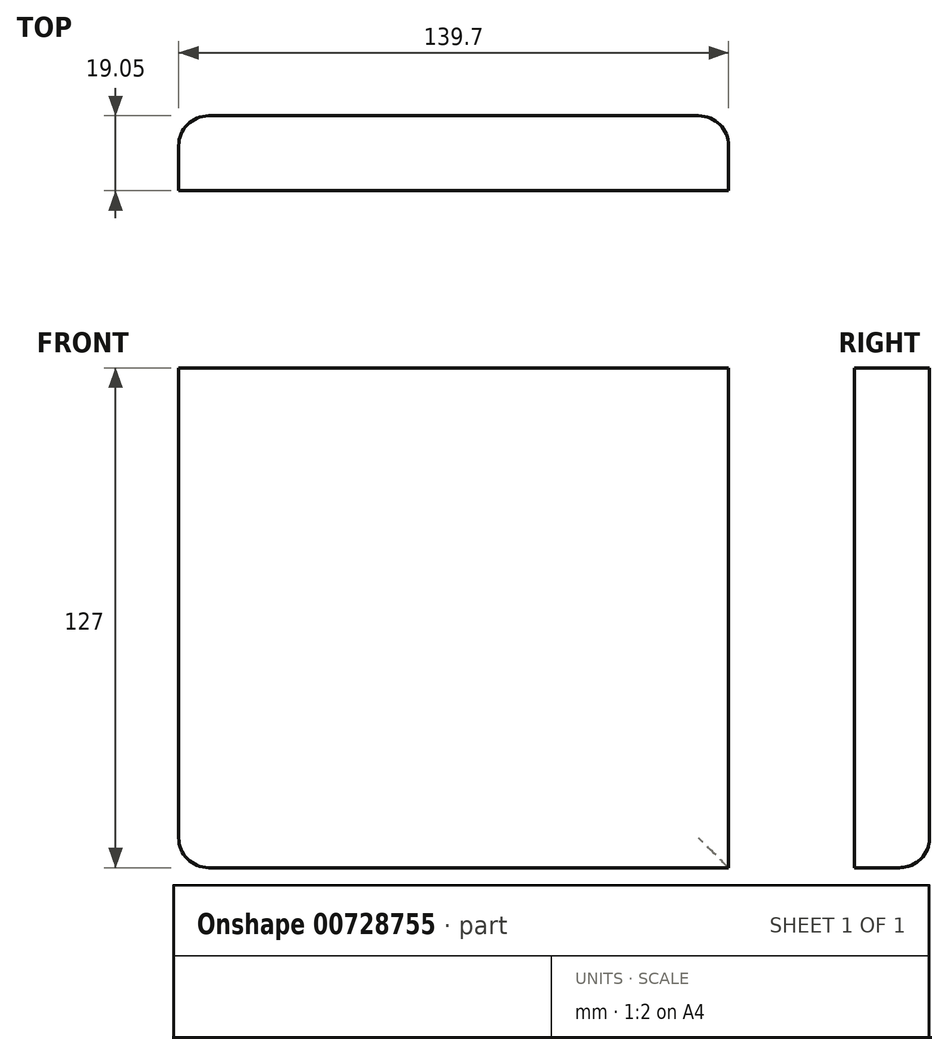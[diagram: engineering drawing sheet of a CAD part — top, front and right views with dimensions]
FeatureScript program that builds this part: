
annotation { "Feature Type Name" : "Feature", "Feature Type Description" : "" }
export const myFeature = defineFeature(function(context is Context, id is Id, definition is map)
    precondition{}
    {
        {
            var Q0;
            Q0=qCreatedBy(makeId("Front.planeOp"),FACE);
            var sketch = newSketch(context, id + "F0", { "sketchPlane" : qUnion([Q0])});
            skLineSegment(sketch, "E0.bottom", {"start": v(69.85, -63.5) * mm, "end": v(-69.85, -63.5) * mm});
            skLineSegment(sketch, "E0.top", {"start": v(69.85, 63.5) * mm, "end": v(-69.85, 63.5) * mm});
            skLineSegment(sketch, "E0.left", {"start": v(69.85, -63.5) * mm, "end": v(69.85, 63.5) * mm});
            skLineSegment(sketch, "E0.right", {"start": v(-69.85, -63.5) * mm, "end": v(-69.85, 63.5) * mm});
            skPoint(sketch, "E0.middle", {"position": v(0, 0) * mm});
            skSolve(sketch);
        }
        {
            var Q0;
            Q0 = qSketchRegion(id + "F0", true);
            extrude(context, id + "F1", {"entities" : qUnion([Q0]), "depth" : 19.05 * mm, "offsetDistance" : 25.4 * mm});
        }
        {
            var Q0;
            Q0=makeQuery(id+"F1.opExtrude","CAP_EDGE",EDGE,{"disambiguationData":[OSD([sQuery(id+"F0.wireOp",EDGE,"E0.left")])],"isStart":true});
            var Q1;
            Q1=makeQuery(id+"F1.opExtrude","CAP_EDGE",EDGE,{"disambiguationData":[OSD([sQuery(id+"F0.wireOp",EDGE,"E0.bottom")])],"isStart":true});
            fillet(context, id + "F2", {"entities" : qUnion([Q0, Q1]), "radius" : 7.62 * mm, "tangentPropagation" : true, "allowEdgeOverflow" : false});
        }
        {
            var Q0;
            Q0=makeQuery(id+"F1.opExtrude","CAP_EDGE",EDGE,{"disambiguationData":[OSD([sQuery(id+"F0.wireOp",EDGE,"E0.right")])],"isStart":true});
            fillet(context, id + "F3", {"entities" : qUnion([Q0]), "radius" : 7.62 * mm, "tangentPropagation" : true, "allowEdgeOverflow" : false});
        }
    });
